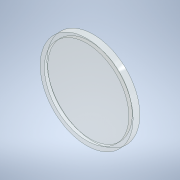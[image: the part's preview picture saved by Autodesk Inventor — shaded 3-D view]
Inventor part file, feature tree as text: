
AUTODESK INVENTOR PART (.ipt)
format: ipt  version: 2022.2 (Build 262287000, 287)  size: 108,032 bytes
history: native  units: mm
features: extrude x2, sketch x1
ambient origin geometry x8: Origin, YZ Plane, XZ Plane, XY Plane, X Axis, Y Axis, Z Axis, Center Point
bodies: Solid1 (feature_tree)
feature tree (3):
  sketch  "Sketch1"  dims[d0=55.0mm d1=50.0mm d2=2.0mm d3=0.0mm d4=2.0mm d5=0.0mm]
  extrude  "Extrusion1"  Depth=2.0mm
  extrude  "Extrusion2"  Depth=2.0mm TaperAngle=0.0deg
